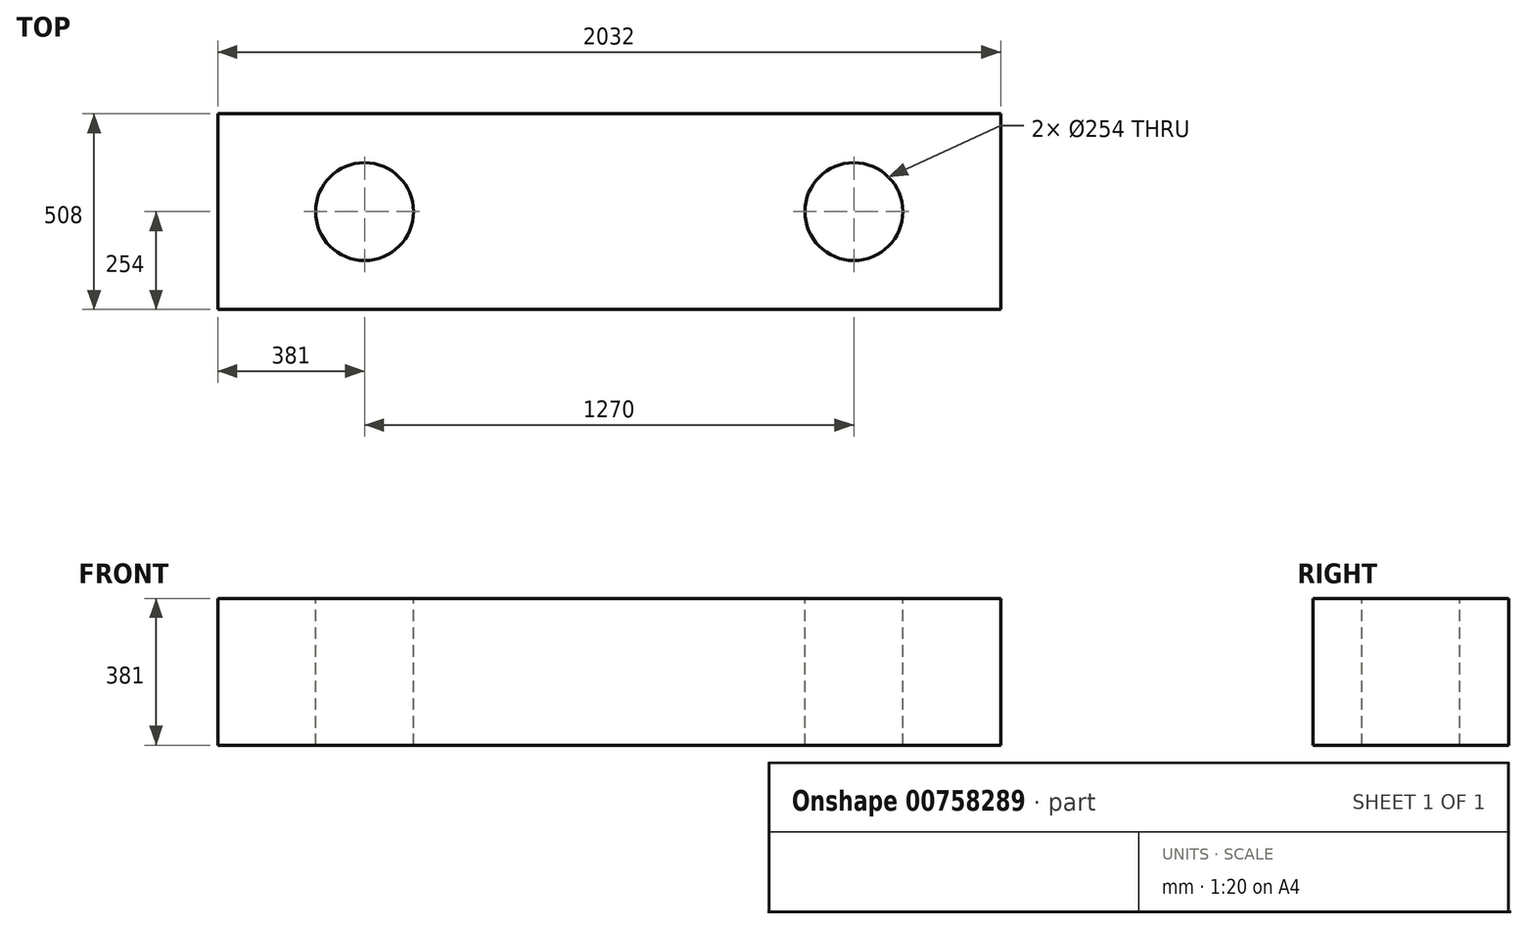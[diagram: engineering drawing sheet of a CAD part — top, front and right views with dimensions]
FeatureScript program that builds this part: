
annotation { "Feature Type Name" : "Feature", "Feature Type Description" : "" }
export const myFeature = defineFeature(function(context is Context, id is Id, definition is map)
    precondition{}
    {
        {
            var Q0;
            Q0=qCreatedBy(makeId("Front.planeOp"),FACE);
            var sketch = newSketch(context, id + "F0", { "sketchPlane" : qUnion([Q0])});
            skLineSegment(sketch, "E0.bottom", {"start": v(0, 0) * mm, "end": v(-2032, 0) * mm});
            skLineSegment(sketch, "E0.top", {"start": v(0, 381) * mm, "end": v(-2032, 381) * mm});
            skLineSegment(sketch, "E0.left", {"start": v(0, 0) * mm, "end": v(0, 381) * mm});
            skLineSegment(sketch, "E0.right", {"start": v(-2032, 0) * mm, "end": v(-2032, 381) * mm});
            skSolve(sketch);
        }
        {
            var Q0;
            Q0 = qSketchRegion(id + "F0", true);
            extrude(context, id + "F1", {"entities" : qUnion([Q0]), "depth" : 508 * mm, "offsetDistance" : 25.4 * mm});
        }
        {
            var Q0;
            Q0=makeQuery(id+"F1.opExtrude","SWEPT_FACE",FACE,{"disambiguationData":[OSD([sQuery(id+"F0.wireOp",EDGE,"E0.top")])]});
            var sketch = newSketch(context, id + "F2", { "sketchPlane" : qUnion([Q0])});
            skLineSegment(sketch, "E1", {"start": v(-2032, 0) * mm, "end": v(-1651, 0) * mm});
            skLineSegment(sketch, "E2", {"start": v(-2032, 0) * mm, "end": v(-2032, -254) * mm});
            skLineSegment(sketch, "E3", {"start": v(-2032, -254) * mm, "end": v(-1651, -254) * mm});
            skLineSegment(sketch, "E4", {"start": v(-1651, 0) * mm, "end": v(-1651, -254) * mm});
            skCircle(sketch, "E5", {"center": v(-1651, -254) * mm, "radius": 127 * mm});
            skLineSegment(sketch, "E6", {"start": v(0, 0) * mm, "end": v(-381, 0) * mm});
            skLineSegment(sketch, "E7", {"start": v(-381, 0) * mm, "end": v(-381, -254) * mm});
            skLineSegment(sketch, "E8", {"start": v(-381, -254) * mm, "end": v(0, -254) * mm});
            skCircle(sketch, "E9", {"center": v(-381, -254) * mm, "radius": 127 * mm});
            skSolve(sketch);
        }
        {
            var Q0;
            {var subQ0=sQuery(id+"F2.wireOp",EDGE,"E4");var subQ1=sQuery(id+"F2.wireOp",EDGE,"E3");var subQ2=makeQuery(id+"F2.imprint","INTERSECT",VERTEX,{"derivedFrom":[subQ1,subQ0]});Q0=makeQuery(id+"F2.imprint","IMPRINT",FACE,{"disambiguationData":[TD([[makeQuery(id+"F2.imprint","IMPRINT",EDGE,{"disambiguationData":[TD([[subQ2,1.0]])],"derivedFrom":subQ1}),-1.0]])]});}
            var Q1;
            {var subQ0=sQuery(id+"F2.wireOp",EDGE,"E4");var subQ1=sQuery(id+"F2.wireOp",EDGE,"E3");var subQ2=makeQuery(id+"F2.imprint","INTERSECT",VERTEX,{"derivedFrom":[subQ1,subQ0]});Q1=makeQuery(id+"F2.imprint","IMPRINT",FACE,{"disambiguationData":[TD([[makeQuery(id+"F2.imprint","IMPRINT",EDGE,{"disambiguationData":[TD([[subQ2,1.0]])],"derivedFrom":subQ1}),1.0]])]});}
            var Q2;
            {var subQ0=sQuery(id+"F2.wireOp",EDGE,"E8");var subQ1=sQuery(id+"F2.wireOp",EDGE,"E7");var subQ2=makeQuery(id+"F2.imprint","INTERSECT",VERTEX,{"derivedFrom":[subQ1,subQ0]});Q2=makeQuery(id+"F2.imprint","IMPRINT",FACE,{"disambiguationData":[TD([[makeQuery(id+"F2.imprint","IMPRINT",EDGE,{"disambiguationData":[TD([[subQ2,1.0]])],"derivedFrom":subQ1}),1.0]])]});}
            var Q3;
            {var subQ0=sQuery(id+"F2.wireOp",EDGE,"E8");var subQ1=sQuery(id+"F2.wireOp",EDGE,"E7");var subQ2=makeQuery(id+"F2.imprint","INTERSECT",VERTEX,{"derivedFrom":[subQ1,subQ0]});Q3=makeQuery(id+"F2.imprint","IMPRINT",FACE,{"disambiguationData":[TD([[makeQuery(id+"F2.imprint","IMPRINT",EDGE,{"disambiguationData":[TD([[subQ2,1.0]])],"derivedFrom":subQ1}),-1.0]])]});}
            extrude(context, id + "F3", {"entities" : qUnion([Q0, Q1, Q2, Q3]), "operationType" : NewBodyOperationType.REMOVE, "oppositeDirection" : true, "depth" : 508 * mm, "offsetDistance" : 25.4 * mm});
        }
    });
